# Revit family: Building-ContenitoriIncasso-GEWISS-48CM-CASSETTE-DERIVAZIONE_INCASSO_GRANDE_CAPACITA_COPERCHIO_ALTO
name_source: partatom
category: Apparecchi elettrici
revit_build: Autodesk Revit 2016 (Build: 20161004_0715(x64)
units: mm (PartAtom-declared; Revit-internal decimal feet)

## family parameters
Condiviso = No
Host = Superficie
Mantenere orientamento annotazione = Sì
Numero OmniClass = 23.80.30.00
Punto di calcolo locali = Sì
Quota connettore circolare = Usa diametro
Taglio con vuoti quando caricato = No
Tipo di parte = Normale
Titolo OmniClass = Distribution Devices

## types (2) — shared parameters
Carico = Altro
Catalogo = BUILDING
Catalogo Serie = 48 CM
Codice Electrocod = 0220
Colore coperchio = Bianco RAL 9016
Glow Wire Test = 650°C
Grado di protezione = IP40
IDF = 8e937d08-6f7d-417d-9762-0c7588212af6
IDT = 885dd1c5-7278-46c8-8c62-00a91bbd3998
Immagine tipo = GW48231.jpg
Installazione = Incasso
Larghezza cassetta interna = 260 mm  [stored 0.853018 ft]
Lunghezza cassetta interna = 520 mm  [stored 1.70604 ft]
Numero di poli = 1
Per Pareti = Muratura
Potenza in wtt = 0 V
Produttore = GEWISS S.p.A.
Prospetto di default = 1219 mm
Resistenza agli urti = IK07
SEO = Cassetta
Scheda Tecnica = https://www.gewiss.com
Temperatura di impiego = -15 +60 °C
Termopressione con biglia = 70 °C
Tipo Materiale = Halogen free secondo norma EN 60754-2
URL = https://www.gewiss.com
Versione file RFA = 18.0
cassetta = <Per categoria>

## per-type parameters (varying)
| type | Codice EAN | Descrizione | Dim. esterne BxHxP (mm) | Modello | Potenza dissipabile (W) | Potenza max dissipabile (W) | Predisposizione scomparti |
| GW48227 - CASSETTA MONTANTI 260X260X121 COP.ALTO | 8011564027305 | CASSETTA MONTANTI 260X260X121 COP.ALTO | 260x260x121 | GW48227 | 13 | 13 | 2 |
| GW48231 - CASSETTA MONTANTI 520X260X121 COP.ALTO | 8011564027312 | CASSETTA MONTANTI 520X260X121 COP.ALTO | 520x260x121 | GW48231 | 30 | 30 | 5 |

note: [stored X ft] marks values corroborated as IEEE doubles in the binary element streams (Revit-internal decimal feet)

## geometry (parser evidence)
native form markers: Blend x2, Sweep x2
no freeform markers — native parametric forms only
